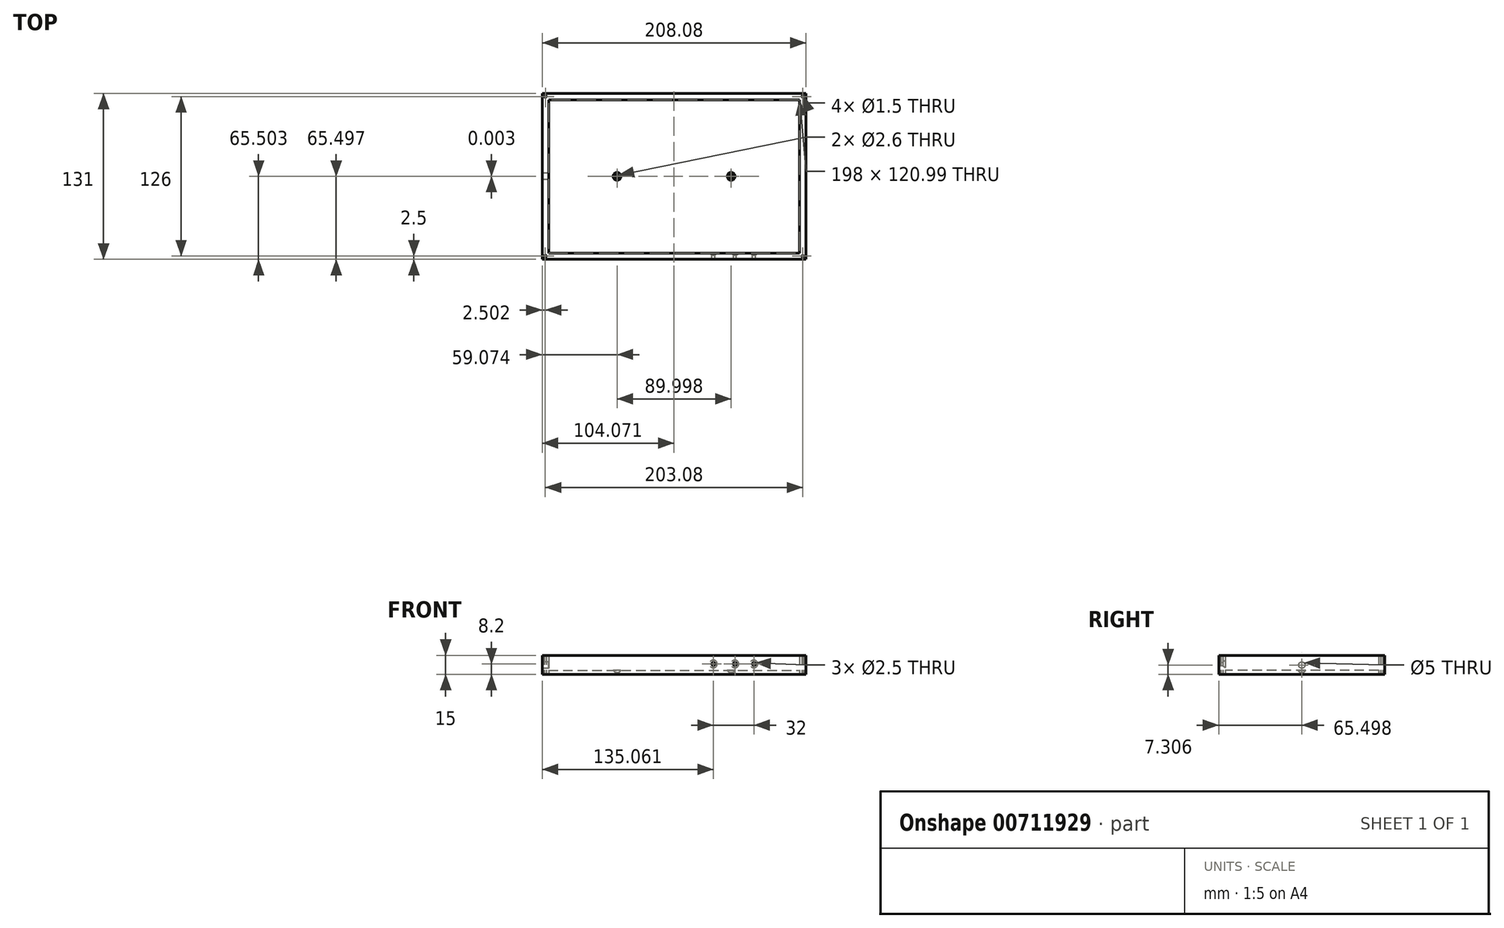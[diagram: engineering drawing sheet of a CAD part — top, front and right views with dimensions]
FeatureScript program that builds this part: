
annotation { "Feature Type Name" : "Feature", "Feature Type Description" : "" }
export const myFeature = defineFeature(function(context is Context, id is Id, definition is map)
    precondition{}
    {
        {
            var Q0;
            Q0=qCreatedBy(makeId("Top.planeOp"),FACE);
            var sketch = newSketch(context, id + "F0", { "sketchPlane" : qUnion([Q0])});
            skLineSegment(sketch, "E0.bottom", {"start": v(-73.22, 60.5) * mm, "end": v(124.78, 60.5) * mm});
            skLineSegment(sketch, "E0.top", {"start": v(-73.22, -60.5) * mm, "end": v(124.78, -60.5) * mm});
            skLineSegment(sketch, "E0.left", {"start": v(-73.22, 60.5) * mm, "end": v(-73.22, -60.5) * mm});
            skLineSegment(sketch, "E0.right", {"start": v(124.78, 60.5) * mm, "end": v(124.78, -60.5) * mm});
            skPoint(sketch, "E1", {"position": v(-19.22, 0) * mm});
            skPoint(sketch, "E2", {"position": v(70.78, 0) * mm});
            skSolve(sketch);
        }
        {
            var Q0;
            Q0 = qSketchRegion(id + "F0", true);
            extrude(context, id + "F1", {"entities" : qUnion([Q0]), "depth" : 3 * mm, "offsetDistance" : 25 * mm});
        }
        {
            var Q0;
            Q0=qCreatedBy(makeId("Top.planeOp"),FACE);
            var sketch = newSketch(context, id + "F2", { "sketchPlane" : qUnion([Q0])});
            skLineSegment(sketch, "E3.bottom", {"start": v(-78.2, 65.5) * mm, "end": v(129.8, 65.5) * mm});
            skLineSegment(sketch, "E3.top", {"start": v(-73.22, 60.5) * mm, "end": v(124.78, 60.5) * mm});
            skLineSegment(sketch, "E4.left", {"start": v(124.78, 60.5) * mm, "end": v(124.78, -60.5) * mm});
            skLineSegment(sketch, "E5.trimOffspring", {"start": v(122.77, 60.5) * mm, "end": v(122.85, 60.5) * mm});
            skLineSegment(sketch, "E6", {"start": v(129.8, 65.5) * mm, "end": v(129.8, -65.5) * mm});
            skPoint(sketch, "E7", {"position": v(-75.7, 63) * mm});
            skPoint(sketch, "E8", {"position": v(127.3, 63) * mm});
            skPoint(sketch, "E9", {"position": v(127.3, -63) * mm});
            skPoint(sketch, "E10", {"position": v(-75.79, -63) * mm});
            skLineSegment(sketch, "E11", {"start": v(-78.29, -65.5) * mm, "end": v(129.8, -65.5) * mm});
            skLineSegment(sketch, "E12", {"start": v(-78.29, -65.5) * mm, "end": v(-78.2, 65.5) * mm});
            skLineSegment(sketch, "E13", {"start": v(124.78, -60.5) * mm, "end": v(-73.2, -60.5) * mm});
            skLineSegment(sketch, "E14", {"start": v(-73.2, -60.5) * mm, "end": v(-73.22, 60.5) * mm});
            skSolve(sketch);
        }
        {
            var Q0;
            Q0 = qSketchRegion(id + "F2", true);
            var Q1;
            Q1 = qSketchRegion(id + "F7", true);
            extrude(context, id + "F3", {"entities" : qUnion([Q0, Q1]), "depth" : 15 * mm, "offsetDistance" : 25 * mm});
        }
        {
            var Q0;
            Q0=makeQuery(id+"F3.opExtrude","SWEPT_FACE",FACE,{"disambiguationData":[OSD([sQuery(id+"F2.wireOp",EDGE,"E12")])]});
            var sketch = newSketch(context, id + "F4", { "sketchPlane" : qUnion([Q0])});
            skCircle(sketch, "E15", {"center": v(0.05, 7.3) * mm, "radius": 3.67 * mm});
            skSolve(sketch);
        }
        {
            var Q0;
            Q0=sQuery(id+"F4.wireOp",VERTEX,"E15.center");
            var Q1;
            Q1=makeQuery(id+"F3.opExtrude","SWEPT_BODY",BODY,{"disambiguationData":[OSD([sQuery(id+"F2.wireOp",EDGE,"E3.bottom"),sQuery(id+"F2.wireOp",EDGE,"E3.top"),sQuery(id+"F2.wireOp",EDGE,"E4.top"),sQuery(id+"F2.wireOp",EDGE,"E4.left"),sQuery(id+"F2.wireOp",EDGE,"rWbC1lUQ-zZys-oqzC-dptY-a8r1G3EkKRGJ.bottom"),sQuery(id+"F2.wireOp",EDGE,"rWbC1lUQ-zZys-oqzC-dptY-a8r1G3EkKRGJ.top"),sQuery(id+"F2.wireOp",EDGE,"rWbC1lUQ-zZys-oqzC-dptY-a8r1G3EkKRGJ.right"),sQuery(id+"F2.wireOp",EDGE,"B7skKctd-R4fH-zRXk-biX4-eaRsuPf59XZ7.left"),sQuery(id+"F2.wireOp",EDGE,"B7skKctd-R4fH-zRXk-biX4-eaRsuPf59XZ7.right"),sQuery(id+"F2.wireOp",EDGE,"finpp0ct-9mIt-r9qb-U4lk-nF6Zjsj66N81"),sQuery(id+"F2.wireOp",EDGE,"E6")])]});
            var Q2;
            Q2=makeQuery(id+"F1.opExtrude","SWEPT_BODY",BODY,{"disambiguationData":[OSD([sQuery(id+"F0.wireOp",EDGE,"E0.bottom"),sQuery(id+"F0.wireOp",EDGE,"E0.top"),sQuery(id+"F0.wireOp",EDGE,"E0.left"),sQuery(id+"F0.wireOp",EDGE,"E0.right")])]});
            hole(context, id + "F5", {"style" : HoleStyle.SIMPLE, "endStyle" : HoleEndStyle.BLIND, "holeDiameter" : 5 * mm, "majorDiameter" : 5 * mm, "holeDepth" : 12 * mm, "isTappedThrough" : true, "tappedDepth" : 12 * mm, "tapClearance" : 3, "locations" : qUnion([Q0]), "scope" : qUnion([Q1, Q2])});
        }
        {
            var Q0;
            Q0=sQuery(id+"F2.wireOp",VERTEX,"E7");
            var Q1;
            Q1=sQuery(id+"F2.wireOp",VERTEX,"E8");
            var Q2;
            Q2=sQuery(id+"F2.wireOp",VERTEX,"E9");
            var Q3;
            Q3=sQuery(id+"F2.wireOp",VERTEX,"E10");
            var Q4;
            Q4=makeQuery(id+"F3.opExtrude","SWEPT_BODY",BODY,{"disambiguationData":[OSD([sQuery(id+"F2.wireOp",EDGE,"E3.bottom"),sQuery(id+"F2.wireOp",EDGE,"E3.top"),sQuery(id+"F2.wireOp",EDGE,"E4.top"),sQuery(id+"F2.wireOp",EDGE,"E4.left"),sQuery(id+"F2.wireOp",EDGE,"rWbC1lUQ-zZys-oqzC-dptY-a8r1G3EkKRGJ.bottom"),sQuery(id+"F2.wireOp",EDGE,"rWbC1lUQ-zZys-oqzC-dptY-a8r1G3EkKRGJ.top"),sQuery(id+"F2.wireOp",EDGE,"rWbC1lUQ-zZys-oqzC-dptY-a8r1G3EkKRGJ.right"),sQuery(id+"F2.wireOp",EDGE,"B7skKctd-R4fH-zRXk-biX4-eaRsuPf59XZ7.left"),sQuery(id+"F2.wireOp",EDGE,"B7skKctd-R4fH-zRXk-biX4-eaRsuPf59XZ7.right"),sQuery(id+"F2.wireOp",EDGE,"finpp0ct-9mIt-r9qb-U4lk-nF6Zjsj66N81"),sQuery(id+"F2.wireOp",EDGE,"E6")])]});
            hole(context, id + "F6", {"style" : HoleStyle.SIMPLE, "endStyle" : HoleEndStyle.THROUGH, "oppositeDirection" : true, "holeDiameter" : 1.5 * mm, "majorDiameter" : 5 * mm, "isTappedThrough" : true, "tappedDepth" : 12 * mm, "tapClearance" : 3, "locations" : qUnion([Q0, Q1, Q2, Q3]), "scope" : qUnion([Q4])});
        }
        {
            var Q0;
            Q0=makeQuery(id+"F3.opExtrude","SWEPT_FACE",FACE,{"disambiguationData":[OSD([sQuery(id+"F2.wireOp",EDGE,"E13")])]});
            var sketch = newSketch(context, id + "F7", { "sketchPlane" : qUnion([Q0])});
            skPoint(sketch, "E16", {"position": v(-88.77, 8.2) * mm});
            skPoint(sketch, "E17", {"position": v(-73.77, 8.2) * mm});
            skPoint(sketch, "E18", {"position": v(-56.77, 8.2) * mm});
            skSolve(sketch);
        }
        {
            var Q0;
            Q0=makeQuery(id+"F1.opExtrude","CAP_FACE",FACE,{"disambiguationData":[OSD([sQuery(id+"F0.wireOp",EDGE,"E0.bottom"),sQuery(id+"F0.wireOp",EDGE,"E0.top"),sQuery(id+"F0.wireOp",EDGE,"E0.left"),sQuery(id+"F0.wireOp",EDGE,"E0.right")])],"isStart":false});
            var sketch = newSketch(context, id + "F8", { "sketchPlane" : qUnion([Q0])});
            skPoint(sketch, "E19", {"position": v(-19.22, 0) * mm});
            skPoint(sketch, "E20", {"position": v(70.78, 0) * mm});
            skSolve(sketch);
        }
        {
            var Q0;
            Q0=sQuery(id+"F8.wireOp",VERTEX,"E19");
            var Q1;
            Q1=sQuery(id+"F8.wireOp",VERTEX,"E20");
            var Q2;
            Q2=makeQuery(id+"F1.opExtrude","SWEPT_BODY",BODY,{"disambiguationData":[OSD([sQuery(id+"F0.wireOp",EDGE,"E0.bottom"),sQuery(id+"F0.wireOp",EDGE,"E0.top"),sQuery(id+"F0.wireOp",EDGE,"E0.left"),sQuery(id+"F0.wireOp",EDGE,"E0.right")])]});
            hole(context, id + "F9", {"style" : HoleStyle.C_SINK, "endStyle" : HoleEndStyle.BLIND, "holeDiameter" : 2.6 * mm, "cSinkDiameter" : 6.2 * mm, "cSinkAngle" : 90 * degree, "majorDiameter" : 5 * mm, "holeDepth" : 10 * mm, "isTappedThrough" : true, "tappedDepth" : 12 * mm, "tapClearance" : 3, "locations" : qUnion([Q0, Q1]), "scope" : qUnion([Q2])});
        }
        {
            var Q0;
            Q0=sQuery(id+"F7.wireOp",VERTEX,"E16");
            var Q1;
            Q1=sQuery(id+"F7.wireOp",VERTEX,"E17");
            var Q2;
            Q2=sQuery(id+"F7.wireOp",VERTEX,"E18");
            var Q3;
            Q3=makeQuery(id+"F3.opExtrude","SWEPT_BODY",BODY,{"disambiguationData":[OSD([sQuery(id+"F2.wireOp",EDGE,"E3.bottom"),sQuery(id+"F2.wireOp",EDGE,"E3.top"),sQuery(id+"F2.wireOp",EDGE,"E4.top"),sQuery(id+"F2.wireOp",EDGE,"E4.left"),sQuery(id+"F2.wireOp",EDGE,"rWbC1lUQ-zZys-oqzC-dptY-a8r1G3EkKRGJ.bottom"),sQuery(id+"F2.wireOp",EDGE,"rWbC1lUQ-zZys-oqzC-dptY-a8r1G3EkKRGJ.top"),sQuery(id+"F2.wireOp",EDGE,"rWbC1lUQ-zZys-oqzC-dptY-a8r1G3EkKRGJ.right"),sQuery(id+"F2.wireOp",EDGE,"B7skKctd-R4fH-zRXk-biX4-eaRsuPf59XZ7.left"),sQuery(id+"F2.wireOp",EDGE,"B7skKctd-R4fH-zRXk-biX4-eaRsuPf59XZ7.right"),sQuery(id+"F2.wireOp",EDGE,"finpp0ct-9mIt-r9qb-U4lk-nF6Zjsj66N81"),sQuery(id+"F2.wireOp",EDGE,"E6")])]});
            hole(context, id + "F10", {"style" : HoleStyle.C_SINK, "endStyle" : HoleEndStyle.BLIND, "holeDiameter" : 2.5 * mm, "cSinkDiameter" : 6 * mm, "cSinkAngle" : 90 * degree, "majorDiameter" : 5 * mm, "holeDepth" : 12 * mm, "isTappedThrough" : true, "tappedDepth" : 12 * mm, "tapClearance" : 3, "locations" : qUnion([Q0, Q1, Q2]), "scope" : qUnion([Q3])});
        }
    });
